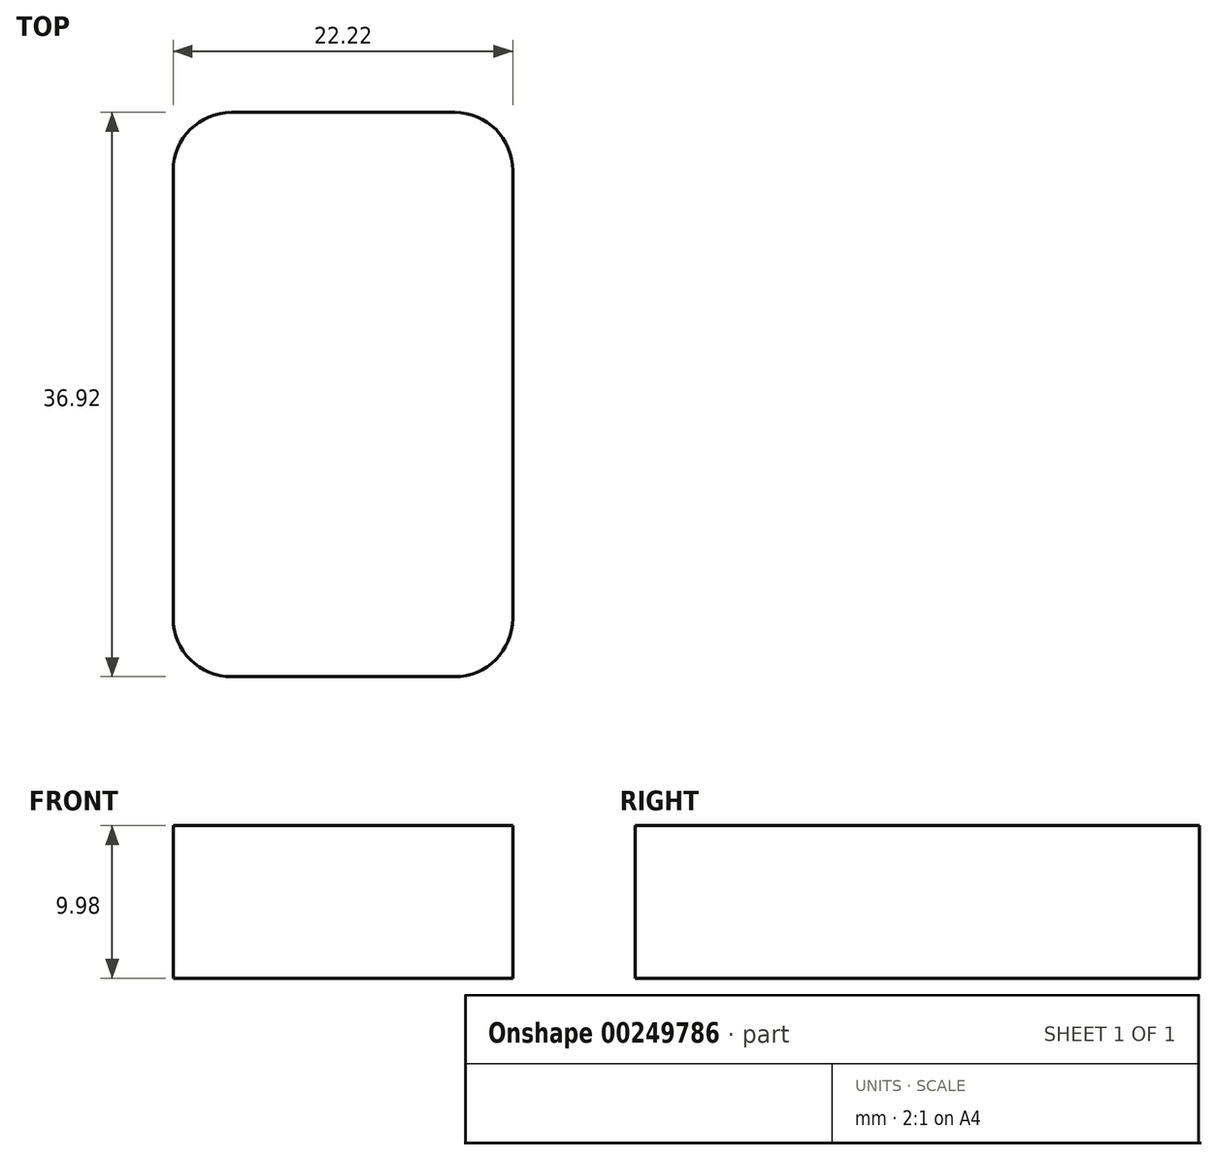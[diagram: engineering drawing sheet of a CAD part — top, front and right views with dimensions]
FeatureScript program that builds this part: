
annotation { "Feature Type Name" : "Feature", "Feature Type Description" : "" }
export const myFeature = defineFeature(function(context is Context, id is Id, definition is map)
    precondition{}
    {
        {
            var Q0;
            Q0=qCreatedBy(makeId("Top.planeOp"),FACE);
            var sketch = newSketch(context, id + "F0", { "sketchPlane" : qUnion([Q0])});
            skLineSegment(sketch, "E0.bottom", {"start": v(-11.11, -18.46) * mm, "end": v(11.11, -18.46) * mm});
            skLineSegment(sketch, "E0.top", {"start": v(-11.11, 18.46) * mm, "end": v(11.11, 18.46) * mm});
            skLineSegment(sketch, "E0.left", {"start": v(-11.11, -18.46) * mm, "end": v(-11.11, 18.46) * mm});
            skLineSegment(sketch, "E0.right", {"start": v(11.11, -18.46) * mm, "end": v(11.11, 18.46) * mm});
            skPoint(sketch, "E0.middle", {"position": v(0, 0) * mm});
            skSolve(sketch);
        }
        {
            var Q0;
            Q0 = qSketchRegion(id + "F0", true);
            extrude(context, id + "F1", {"entities" : qUnion([Q0]), "depth" : 9.98 * mm});
        }
        {
            var Q0;
            Q0=makeQuery(id+"F1.opExtrude","SWEPT_EDGE",EDGE,{"disambiguationData":[OSD([sQuery(id+"F0.wireOp",EDGE,"E0.bottom"),sQuery(id+"F0.wireOp",EDGE,"E0.left")])]});
            var Q1;
            Q1=makeQuery(id+"F1.opExtrude","SWEPT_EDGE",EDGE,{"disambiguationData":[OSD([sQuery(id+"F0.wireOp",EDGE,"E0.top"),sQuery(id+"F0.wireOp",EDGE,"E0.left")])]});
            var Q2;
            Q2=makeQuery(id+"F1.opExtrude","SWEPT_EDGE",EDGE,{"disambiguationData":[OSD([sQuery(id+"F0.wireOp",EDGE,"E0.top"),sQuery(id+"F0.wireOp",EDGE,"E0.right")])]});
            var Q3;
            Q3=makeQuery(id+"F1.opExtrude","SWEPT_EDGE",EDGE,{"disambiguationData":[OSD([sQuery(id+"F0.wireOp",EDGE,"E0.bottom"),sQuery(id+"F0.wireOp",EDGE,"E0.right")])]});
            fillet(context, id + "F2", {"entities" : qUnion([Q0, Q1, Q2, Q3]), "radius" : 3.8 * mm, "tangentPropagation" : true, "allowEdgeOverflow" : false});
        }
    });
